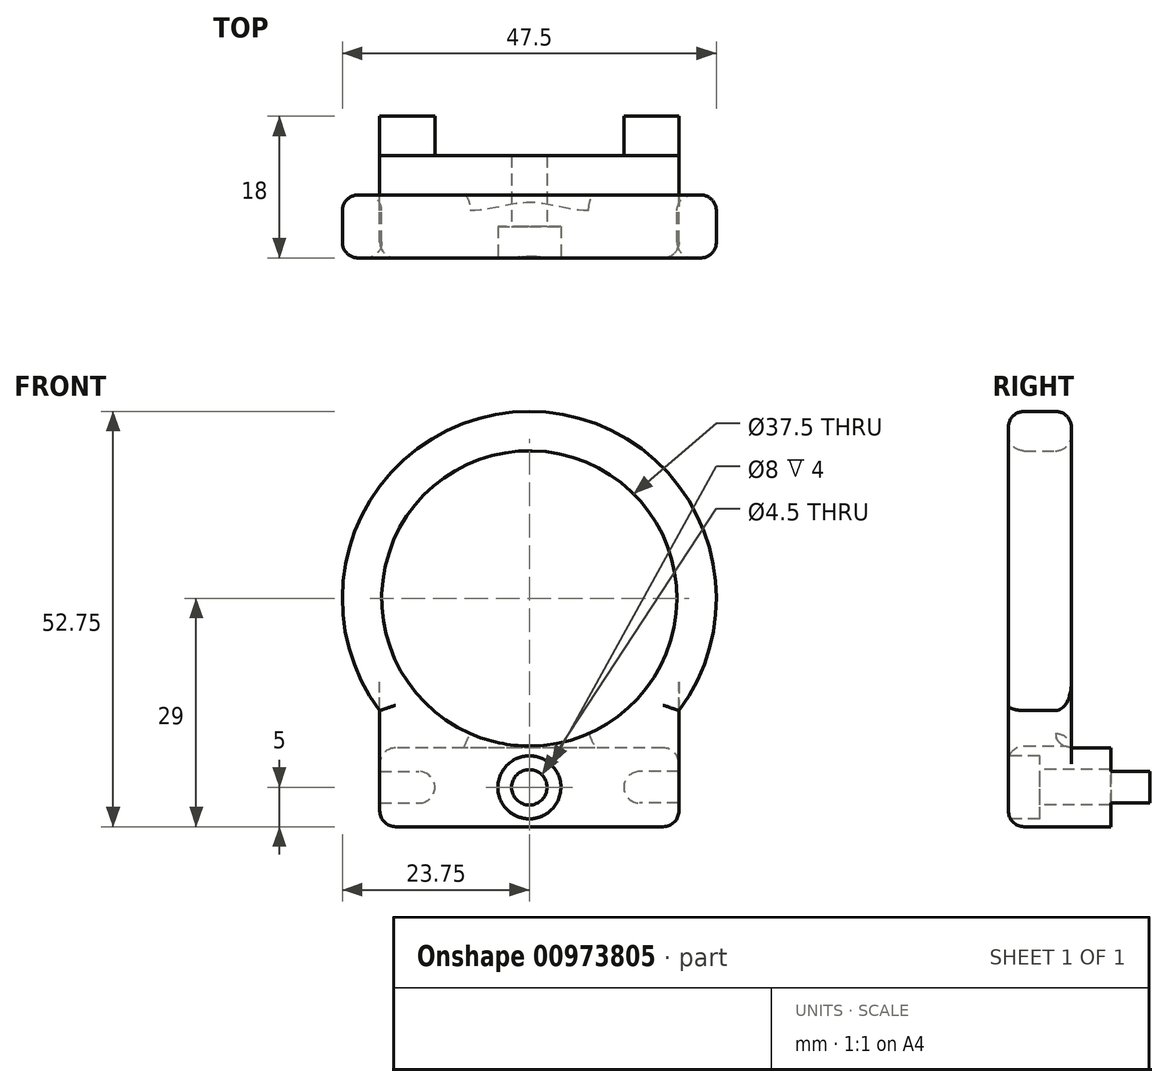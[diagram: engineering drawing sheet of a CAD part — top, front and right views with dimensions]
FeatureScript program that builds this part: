
annotation { "Feature Type Name" : "Feature", "Feature Type Description" : "" }
export const myFeature = defineFeature(function(context is Context, id is Id, definition is map)
    precondition{}
    {
        {
            var Q0;
            Q0=qCreatedBy(makeId("Front.planeOp"),FACE);
            var sketch = newSketch(context, id + "F0", { "sketchPlane" : qUnion([Q0])});
            skLineSegment(sketch, "E0.bottom", {"start": v(0, 0) * mm, "end": v(-38, 0) * mm, "construction": true});
            skLineSegment(sketch, "E0.top", {"start": v(0, 10) * mm, "end": v(-38, 10) * mm, "construction": true});
            skLineSegment(sketch, "E0.left", {"start": v(0, 0) * mm, "end": v(0, 10) * mm, "construction": true});
            skLineSegment(sketch, "E0.right", {"start": v(-38, 0) * mm, "end": v(-38, 10) * mm, "construction": true});
            skCircle(sketch, "E1", {"center": v(-19, 29) * mm, "radius": 19 * mm, "construction": true});
            skPoint(sketch, "E1.centerSnap0", {"position": v(-19, 10) * mm});
            skLineSegment(sketch, "E2", {"start": v(-38, 10) * mm, "end": v(-38, 29) * mm, "construction": true});
            skLineSegment(sketch, "E3", {"start": v(0, 10) * mm, "end": v(0, 29) * mm, "construction": true});
            skSolve(sketch);
        }
        {
            var Q0;
            Q0=qCreatedBy(makeId("Front.planeOp"),FACE);
            var sketch = newSketch(context, id + "F1", { "sketchPlane" : qUnion([Q0])});
            skLineSegment(sketch, "E4.bottom", {"start": v(0, 0) * mm, "end": v(-38, 0) * mm});
            skCircle(sketch, "E5", {"center": v(-19, 29) * mm, "radius": 18.75 * mm});
            skArc(sketch, "E6", {"start": v(0, 14.75) * mm, "mid": v(-19, 52.75) * mm, "end": v(-38, 14.75) * mm});
            skLineSegment(sketch, "E7", {"start": v(0, 0) * mm, "end": v(0, 14.75) * mm});
            skLineSegment(sketch, "E8", {"start": v(-38, 0) * mm, "end": v(-38, 14.75) * mm});
            skSolve(sketch);
        }
        {
            var Q0;
            Q0 = qSketchRegion(id + "F1", true);
            extrude(context, id + "F2", {"entities" : qUnion([Q0]), "depth" : 8 * mm, "offsetDistance" : 25 * mm});
        }
        {
            var Q0;
            Q0=makeQuery(id+"F2.opExtrude","CAP_FACE",FACE,{"disambiguationData":[OSD([sQuery(id+"F1.wireOp",EDGE,"E4.bottom"),sQuery(id+"F1.wireOp",EDGE,"E5"),sQuery(id+"F1.wireOp",EDGE,"E6")])],"isStart":true});
            var sketch = newSketch(context, id + "F3", { "sketchPlane" : qUnion([Q0])});
            skLineSegment(sketch, "E9.bottom", {"start": v(0, 0) * mm, "end": v(38, 0) * mm});
            skLineSegment(sketch, "E9.top", {"start": v(0, 10) * mm, "end": v(38, 10) * mm});
            skLineSegment(sketch, "E9.left", {"start": v(0, 0) * mm, "end": v(0, 10) * mm});
            skLineSegment(sketch, "E9.right", {"start": v(38, 0) * mm, "end": v(38, 10) * mm});
            skSolve(sketch);
        }
        {
            var Q0;
            Q0=makeQuery(id+"F3.imprint","IMPRINT",FACE,{"disambiguationData":[TD([[makeQuery(id+"F3.imprint","IMPRINT",EDGE,{"derivedFrom":sQuery(id+"F3.wireOp",EDGE,"E9.bottom")}),1.0]])]});
            extrude(context, id + "F4", {"entities" : qUnion([Q0]), "operationType" : NewBodyOperationType.ADD, "depth" : 5 * mm, "offsetDistance" : 25 * mm});
        }
        {
            var Q0;
            Q0=makeQuery(id+"F4.opExtrude","CAP_FACE",FACE,{"disambiguationData":[OSD([sQuery(id+"F3.wireOp",EDGE,"E9.bottom"),sQuery(id+"F3.wireOp",EDGE,"E9.top"),sQuery(id+"F3.wireOp",EDGE,"E9.left"),sQuery(id+"F3.wireOp",EDGE,"E9.right")])],"isStart":false});
            var sketch = newSketch(context, id + "F5", { "sketchPlane" : qUnion([Q0])});
            skLineSegment(sketch, "E10.bottom", {"start": v(0, 7) * mm, "end": v(7, 7) * mm});
            skLineSegment(sketch, "E10.top", {"start": v(0, 3) * mm, "end": v(7, 3) * mm});
            skLineSegment(sketch, "E10.left", {"start": v(0, 7) * mm, "end": v(0, 3) * mm});
            skLineSegment(sketch, "E10.right", {"start": v(7, 7) * mm, "end": v(7, 3) * mm});
            skLineSegment(sketch, "E11.bottom", {"start": v(38, 7) * mm, "end": v(31, 7) * mm});
            skLineSegment(sketch, "E11.top", {"start": v(38, 3) * mm, "end": v(31, 3) * mm});
            skLineSegment(sketch, "E11.left", {"start": v(38, 7) * mm, "end": v(38, 3) * mm});
            skLineSegment(sketch, "E11.right", {"start": v(31, 7) * mm, "end": v(31, 3) * mm});
            skSolve(sketch);
        }
        {
            var Q0;
            Q0 = qSketchRegion(id + "F5", true);
            extrude(context, id + "F6", {"entities" : qUnion([Q0]), "operationType" : NewBodyOperationType.ADD, "depth" : 5 * mm, "offsetDistance" : 25 * mm});
        }
        {
            var Q0;
            Q0=makeQuery(id+"F2.opExtrude","CAP_FACE",FACE,{"disambiguationData":[OSD([sQuery(id+"F1.wireOp",EDGE,"E4.bottom"),sQuery(id+"F1.wireOp",EDGE,"E5"),sQuery(id+"F1.wireOp",EDGE,"E6")])],"isStart":false});
            var sketch = newSketch(context, id + "F7", { "sketchPlane" : qUnion([Q0])});
            skCircle(sketch, "E12", {"center": v(-19, 5) * mm, "radius": 4 * mm});
            skPoint(sketch, "E13", {"position": v(-19, 0) * mm});
            skSolve(sketch);
        }
        {
            var Q0;
            Q0 = qSketchRegion(id + "F7", true);
            extrude(context, id + "F8", {"entities" : qUnion([Q0]), "operationType" : NewBodyOperationType.REMOVE, "oppositeDirection" : true, "depth" : 4 * mm, "offsetDistance" : 25 * mm});
        }
        {
            var Q0;
            Q0=makeQuery(id+"F8.boolean.opBoolean","COPY",FACE,{"derivedFrom":makeQuery(id+"F8.opExtrude","CAP_FACE",FACE,{"disambiguationData":[OSD([sQuery(id+"F7.wireOp",EDGE,"E12")])],"isStart":false})});
            var sketch = newSketch(context, id + "F9", { "sketchPlane" : qUnion([Q0])});
            skCircle(sketch, "E14", {"center": v(-19, 5) * mm, "radius": 2.25 * mm});
            skSolve(sketch);
        }
        {
            var Q0;
            Q0 = qSketchRegion(id + "F9", true);
            var Q1;
            Q1=makeQuery(id+"F4.opExtrude","CAP_FACE",FACE,{"disambiguationData":[OSD([sQuery(id+"F3.wireOp",EDGE,"E9.bottom"),sQuery(id+"F3.wireOp",EDGE,"E9.top"),sQuery(id+"F3.wireOp",EDGE,"E9.left"),sQuery(id+"F3.wireOp",EDGE,"E9.right")])],"isStart":false});
            extrude(context, id + "F10", {"entities" : qUnion([Q0]), "operationType" : NewBodyOperationType.REMOVE, "endBound" : BoundingType.UP_TO_SURFACE, "oppositeDirection" : true, "depth" : 25 * mm, "endBoundEntityFace" : qUnion([Q1]), "offsetDistance" : 25 * mm});
        }
        {
            var Q0;
            Q0=makeQuery(id+"F2.opExtrude","CAP_EDGE",EDGE,{"disambiguationData":[OSD([sQuery(id+"F1.wireOp",EDGE,"E5")])],"isStart":true});
            var Q1;
            Q1=makeQuery(id+"F2.opExtrude","CAP_EDGE",EDGE,{"disambiguationData":[OSD([sQuery(id+"F1.wireOp",EDGE,"E5")])],"isStart":false});
            var Q2;
            Q2=makeQuery(id+"F2.opExtrude","CAP_EDGE",EDGE,{"disambiguationData":[OSD([sQuery(id+"F1.wireOp",EDGE,"E6")])],"isStart":true});
            var Q3;
            Q3=makeQuery(id+"F2.opExtrude","CAP_EDGE",EDGE,{"disambiguationData":[OSD([sQuery(id+"F1.wireOp",EDGE,"E6")])],"isStart":false});
            var Q4;
            Q4=makeQuery(id+"F2.opExtrude","CAP_EDGE",EDGE,{"disambiguationData":[OSD([sQuery(id+"F1.wireOp",EDGE,"E4.bottom")])],"isStart":false});
            var Q5;
            Q5=makeQuery(id+"F6.opExtrude","SWEPT_EDGE",EDGE,{"disambiguationData":[OSD([sQuery(id+"F5.wireOp",EDGE,"E11.bottom"),sQuery(id+"F5.wireOp",EDGE,"E11.right")])]});
            var Q6;
            Q6=makeQuery(id+"F6.opExtrude","SWEPT_EDGE",EDGE,{"disambiguationData":[OSD([sQuery(id+"F5.wireOp",EDGE,"E10.bottom"),sQuery(id+"F5.wireOp",EDGE,"E10.right")])]});
            var Q7;
            Q7=makeQuery(id+"F6.opExtrude","SWEPT_EDGE",EDGE,{"disambiguationData":[OSD([sQuery(id+"F5.wireOp",EDGE,"E10.top"),sQuery(id+"F5.wireOp",EDGE,"E10.right")])]});
            var Q8;
            Q8=makeQuery(id+"F6.opExtrude","SWEPT_EDGE",EDGE,{"disambiguationData":[OSD([sQuery(id+"F5.wireOp",EDGE,"E11.top"),sQuery(id+"F5.wireOp",EDGE,"E11.right")])]});
            var Q9;
            Q9=makeQuery(id+"F4.opExtrude","SWEPT_EDGE",EDGE,{"disambiguationData":[OSD([sQuery(id+"F3.wireOp",EDGE,"E9.top"),sQuery(id+"F3.wireOp",EDGE,"E9.left")])]});
            var Q10;
            Q10=makeQuery(id+"F4.opExtrude","SWEPT_EDGE",EDGE,{"disambiguationData":[OSD([sQuery(id+"F3.wireOp",EDGE,"E9.top"),sQuery(id+"F3.wireOp",EDGE,"E9.right")])]});
            fillet(context, id + "F11", {"entities" : qUnion([Q0, Q1, Q2, Q3, Q4, Q5, Q6, Q7, Q8, Q9, Q10]), "radius" : 2 * mm, "tangentPropagation" : true, "allowEdgeOverflow" : false});
        }
        {
            var Q0;
            Q0=makeQuery(id+"F4.opExtrude","SWEPT_EDGE",EDGE,{"disambiguationData":[OSD([sQuery(id+"F1.wireOp",EDGE,"E6"),sQuery(id+"F3.wireOp",EDGE,"E9.bottom"),sQuery(id+"F3.wireOp",EDGE,"E9.right")])]});
            var Q1;
            Q1=makeQuery(id+"F4.opExtrude","SWEPT_EDGE",EDGE,{"disambiguationData":[OSD([sQuery(id+"F1.wireOp",EDGE,"E6"),sQuery(id+"F3.wireOp",EDGE,"E9.bottom"),sQuery(id+"F3.wireOp",EDGE,"E9.left")])]});
            fillet(context, id + "F12", {"entities" : qUnion([Q0, Q1]), "radius" : 2 * mm, "tangentPropagation" : true, "allowEdgeOverflow" : false});
        }
    });
